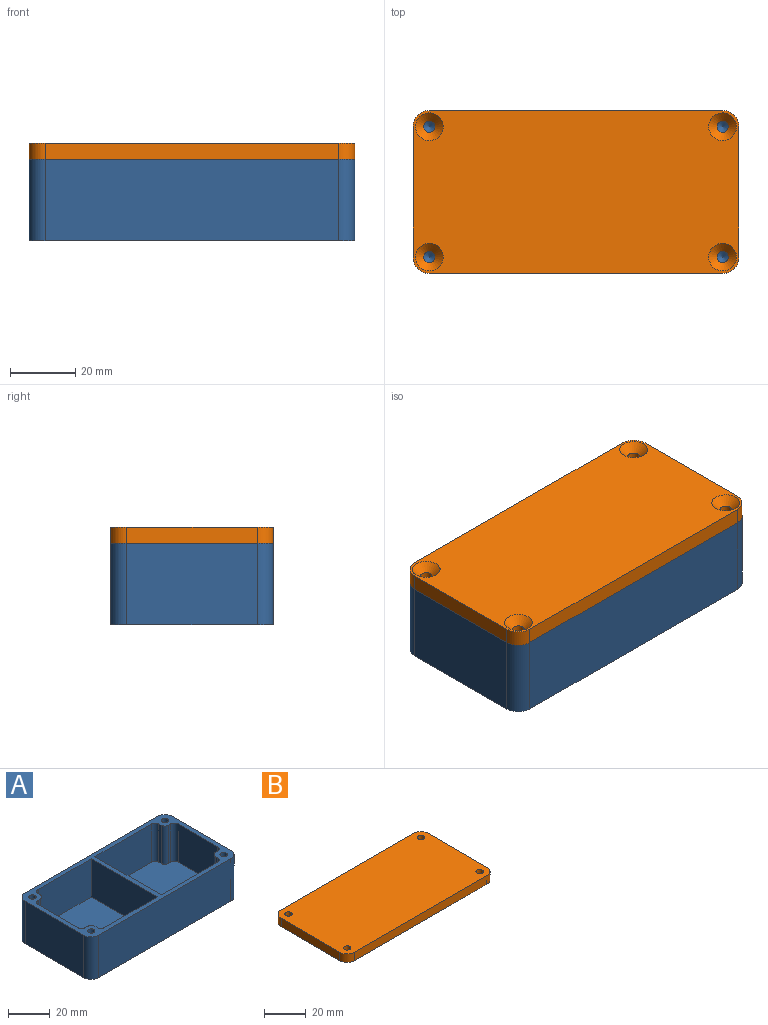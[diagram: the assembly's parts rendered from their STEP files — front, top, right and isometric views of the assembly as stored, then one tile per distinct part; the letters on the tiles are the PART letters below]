
ASSEMBLY  parts=2 mates=1
PART A: 48 faces, bbox 100x50x25 mm
  f0: cone r=0mm half-angle=59deg, axis (0,0,1), area 11.2mm2, adj f1
  f1: cylinder r=1.75mm len=12mm, axis (0,0,1), area 131.9mm2, adj f0,f14
  f2: cone r=0mm half-angle=59deg, axis (0,0,1), area 11.2mm2, adj f3
  f3: cylinder r=1.75mm len=12mm, axis (0,0,1), area 131.9mm2, adj f2,f14
  f4: cone r=0mm half-angle=59deg, axis (0,0,1), area 11.2mm2, adj f5
  f5: cylinder r=1.75mm len=12mm, axis (0,0,1), area 131.9mm2, adj f4,f14
  f6: plane 47.5x45mm, normal (0,0,1), area 2050.3mm2, adj f7,f8,f9,f20,f32,f33,f34,f35
  f7: plane 38.5x22.5mm, normal (0,1,0), area 866.2mm2, adj f6,f14,f20,f38
  f8: plane 27x22.5mm, normal (-1,0,0), area 607.5mm2, adj f6,f14,f36,f41
  f9: plane 38.5x22.5mm, normal (0,-1,0), area 866.2mm2, adj f6,f14,f20,f40
  f10: plane 45x45mm, normal (0,0,1), area 1937.8mm2, adj f11,f12,f13,f21,f22,f23,f24,f25
  f11: plane 27x22.5mm, normal (1,0,0), area 607.5mm2, adj f10,f14,f42,f47
  f12: plane 36x22.5mm, normal (0,1,0), area 810mm2, adj f10,f14,f21,f46
  f13: plane 36x22.5mm, normal (0,-1,0), area 810mm2, adj f10,f14,f21,f44
  f14: plane 100x50mm, normal (0,0,1), area 951.9mm2, adj f1,f3,f5,f7,f8,f9,f11,f12
  f15: plane 40x25mm, normal (-1,0,0), area 1000mm2, adj f14,f19,f28,f31
  f16: plane 90x25mm, normal (0,-1,0), area 2250mm2, adj f14,f19,f28,f29
  f17: plane 40x25mm, normal (1,0,0), area 1000mm2, adj f14,f19,f29,f30
  f18: plane 90x25mm, normal (0,1,0), area 2250mm2, adj f14,f19,f30,f31
  f19: plane 100x50mm, normal (0,0,-1), area 4978.5mm2, adj f15,f16,f17,f18,f28,f29,f30,f31
  f20: plane 45x22.5mm, normal (1,0,0), area 1012.5mm2, adj f6,f7,f9,f14
  f21: plane 45x22.5mm, normal (-1,0,0), area 1012.5mm2, adj f10,f12,f13,f14
  f22: plane 22.5x1.5mm, normal (0,1,0), area 33.7mm2, adj f10,f14,f45,f47
  f23: plane 22.5x1.5mm, normal (1,0,0), area 33.7mm2, adj f10,f14,f45,f46
  f24: plane 22.5x1.5mm, normal (0,-1,0), area 33.7mm2, adj f10,f14,f42,f43
  f25: plane 22.5x1.5mm, normal (1,0,0), area 33.8mm2, adj f10,f14,f43,f44
  f26: cone r=0mm half-angle=59deg, axis (0,0,1), area 11.2mm2, adj f27
  f27: cylinder r=1.75mm len=12mm, axis (0,0,1), area 131.9mm2, adj f14,f26
  f28: cylinder r=5mm len=25mm, axis (0,0,1), area 196.3mm2, adj f14,f15,f16,f19
  f29: cylinder r=5mm len=25mm, axis (0,0,-1), area 196.3mm2, adj f14,f16,f17,f19
  f30: cylinder r=5mm len=25mm, axis (0,0,1), area 196.3mm2, adj f14,f17,f18,f19
  f31: cylinder r=5mm len=25mm, axis (0,0,-1), area 196.3mm2, adj f14,f15,f18,f19
  f32: plane 22.5x1.5mm, normal (0,-1,0), area 33.8mm2, adj f6,f14,f39,f41
  f33: plane 22.5x1.5mm, normal (-1,0,0), area 33.8mm2, adj f6,f14,f39,f40
  f34: plane 22.5x1.5mm, normal (0,1,0), area 33.8mm2, adj f6,f14,f36,f37
  f35: plane 22.5x1.5mm, normal (-1,0,0), area 33.7mm2, adj f6,f14,f37,f38
  f36: cylinder r=2.5mm len=22.5mm, axis (0,0,-1), area 88.4mm2, adj f6,f8,f14,f34
  f37: cylinder r=2.5mm len=22.5mm, axis (0,0,1), area 88.4mm2, adj f6,f14,f34,f35
  f38: cylinder r=2.5mm len=22.5mm, axis (0,0,1), area 88.4mm2, adj f6,f7,f14,f35
  f39: cylinder r=2.5mm len=22.5mm, axis (0,0,1), area 88.4mm2, adj f6,f14,f32,f33
  f40: cylinder r=2.5mm len=22.5mm, axis (0,0,1), area 88.4mm2, adj f6,f9,f14,f33
  f41: cylinder r=2.5mm len=22.5mm, axis (0,0,1), area 88.4mm2, adj f6,f8,f14,f32
  f42: cylinder r=2.5mm len=22.5mm, axis (0,0,1), area 88.4mm2, adj f10,f11,f14,f24
  f43: cylinder r=2.5mm len=22.5mm, axis (0,0,1), area 88.4mm2, adj f10,f14,f24,f25
  f44: cylinder r=2.5mm len=22.5mm, axis (0,0,-1), area 88.4mm2, adj f10,f13,f14,f25
  f45: cylinder r=2.5mm len=22.5mm, axis (0,0,1), area 88.4mm2, adj f10,f14,f22,f23
  f46: cylinder r=2.5mm len=22.5mm, axis (0,0,-1), area 88.4mm2, adj f10,f12,f14,f23
  f47: cylinder r=2.5mm len=22.5mm, axis (0,0,-1), area 88.4mm2, adj f10,f11,f14,f22
PART B: 18 faces, bbox 100x50x5 mm
  f0: cone r=1.75mm half-angle=45deg, axis (0,0,-1), area 66.6mm2, adj f1,f11
  f1: cylinder r=1.75mm len=3.5mm, axis (0,0,-1), area 27.5mm2, adj f0,f10
  f2: cone r=1.75mm half-angle=45deg, axis (0,0,-1), area 66.6mm2, adj f3,f11
  f3: cylinder r=1.75mm len=3.5mm, axis (0,0,-1), area 27.5mm2, adj f2,f10
  f4: cone r=1.75mm half-angle=45deg, axis (0,0,-1), area 66.6mm2, adj f5,f11
  f5: cylinder r=1.75mm len=3.5mm, axis (0,0,-1), area 27.5mm2, adj f4,f10
  f6: plane 40x5mm, normal (-1,0,0), area 200mm2, adj f10,f11,f14,f17
  f7: plane 90x5mm, normal (0,-1,0), area 450mm2, adj f10,f11,f14,f15
  f8: plane 40x5mm, normal (1,0,0), area 200mm2, adj f10,f11,f15,f16
  f9: plane 90x5mm, normal (0,1,0), area 450mm2, adj f10,f11,f16,f17
  f10: plane 100x50mm, normal (0,0,1), area 4940.1mm2, adj f1,f3,f5,f6,f7,f8,f9,f12
  f11: plane 100x50mm, normal (0,0,-1), area 4751.6mm2, adj f0,f2,f4,f6,f7,f8,f9,f13
  f12: cylinder r=1.75mm len=3.5mm, axis (0,0,-1), area 27.5mm2, adj f10,f13
  f13: cone r=1.75mm half-angle=45deg, axis (0,0,-1), area 66.6mm2, adj f11,f12
  f14: cylinder r=5mm len=5mm, axis (0,0,1), area 39.3mm2, adj f6,f7,f10,f11
  f15: cylinder r=5mm len=5mm, axis (0,0,-1), area 39.3mm2, adj f7,f8,f10,f11
  f16: cylinder r=5mm len=5mm, axis (0,0,1), area 39.3mm2, adj f8,f9,f10,f11
  f17: cylinder r=5mm len=5mm, axis (0,0,-1), area 39.3mm2, adj f6,f9,f10,f11
PLACE A t=(-4,7.42,-4.81)mm
PLACE B rot(axis=(1,0,0),180deg) t=(-4,57.42,25.19)mm
MATE slider A.f26 <-> B.f2  axis (0,0,1) through (1,12.42,20.19)mm
